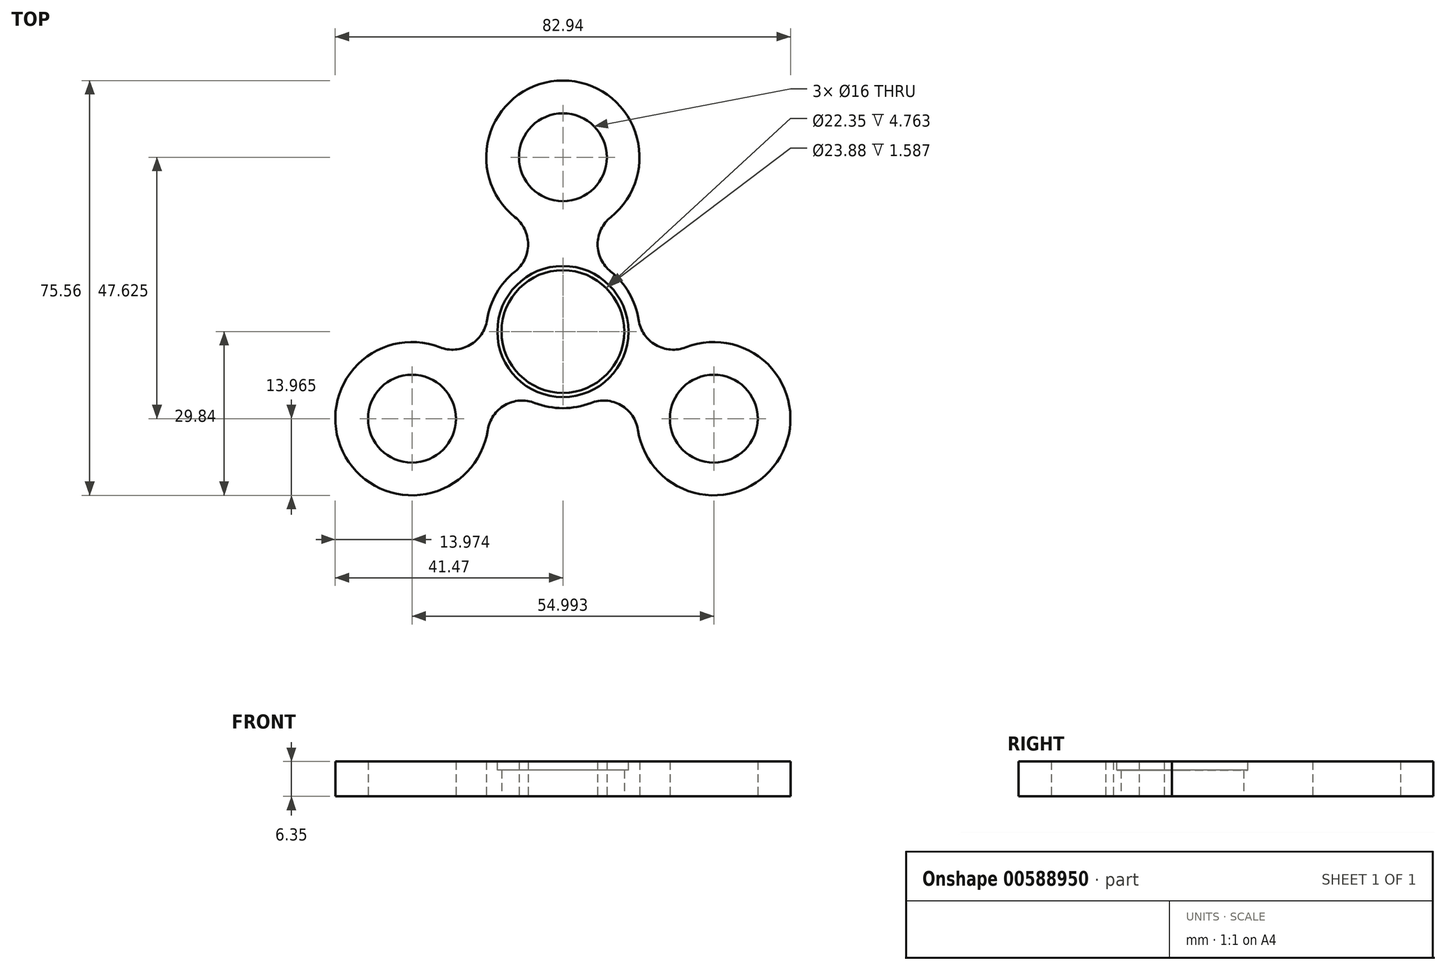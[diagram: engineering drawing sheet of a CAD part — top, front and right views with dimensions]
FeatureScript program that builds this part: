
annotation { "Feature Type Name" : "Feature", "Feature Type Description" : "" }
export const myFeature = defineFeature(function(context is Context, id is Id, definition is map)
    precondition{}
    {
        {
            var Q0;
            Q0=qCreatedBy(makeId("Top.planeOp"),FACE);
            var sketch = newSketch(context, id + "F0", { "sketchPlane" : qUnion([Q0])});
            skCircle(sketch, "E0", {"center": v(0, 0) * mm, "radius": 11.18 * mm});
            skArc(sketch, "E1", {"start": v(-8.72, 10.91) * mm, "mid": v(-12.1, 6.98) * mm, "end": v(-13.81, 2.1) * mm});
            skCircle(sketch, "E2", {"center": v(0, 31.75) * mm, "radius": 8 * mm});
            skArc(sketch, "E3", {"start": v(8.72, 20.84) * mm, "mid": v(0, 45.72) * mm, "end": v(-8.72, 20.84) * mm});
            skArc(sketch, "E4", {"start": v(-8.72, 10.91) * mm, "mid": v(-6.33, 15.87) * mm, "end": v(-8.72, 20.84) * mm});
            skArc(sketch, "E5.MirrorCS", {"start": v(8.72, 10.91) * mm, "mid": v(6.33, 15.87) * mm, "end": v(8.72, 20.84) * mm});
            skArc(sketch, "E6.1.0", {"start": v(-13.81, 2.1) * mm, "mid": v(-16.92, -2.45) * mm, "end": v(-22.4, -2.87) * mm});
            skArc(sketch, "E6.1.1", {"start": v(-5.1, -13) * mm, "mid": v(-10.58, -13.42) * mm, "end": v(-13.68, -17.97) * mm});
            skArc(sketch, "E6.1.2", {"start": v(-22.4, -2.87) * mm, "mid": v(-39.6, -22.86) * mm, "end": v(-13.68, -17.97) * mm});
            skCircle(sketch, "E6.1.3", {"center": v(-27.5, -15.87) * mm, "radius": 8 * mm});
            skArc(sketch, "E6.2.0", {"start": v(5.1, -13) * mm, "mid": v(10.58, -13.42) * mm, "end": v(13.68, -17.97) * mm});
            skArc(sketch, "E6.2.1", {"start": v(13.81, 2.1) * mm, "mid": v(16.92, -2.45) * mm, "end": v(22.4, -2.87) * mm});
            skArc(sketch, "E6.2.2", {"start": v(13.68, -17.97) * mm, "mid": v(39.6, -22.86) * mm, "end": v(22.4, -2.87) * mm});
            skCircle(sketch, "E6.2.3", {"center": v(27.5, -15.88) * mm, "radius": 8 * mm});
            skArc(sketch, "E7.trimOffspring", {"start": v(13.81, 2.1) * mm, "mid": v(12.1, 6.98) * mm, "end": v(8.72, 10.91) * mm});
            skArc(sketch, "E8.trimOffspring", {"start": v(-5.1, -13) * mm, "mid": v(0, -13.97) * mm, "end": v(5.1, -13) * mm});
            skSolve(sketch);
        }
        {
            var Q0;
            Q0=makeQuery(id+"F0.imprint","IMPRINT",FACE,{"disambiguationData":[TD([[makeQuery(id+"F0.imprint","IMPRINT",EDGE,{"derivedFrom":sQuery(id+"F0.wireOp",EDGE,"E0")}),-1.0]])]});
            extrude(context, id + "F1", {"entities" : qUnion([Q0]), "depth" : 6.35 * mm, "offsetDistance" : 25.4 * mm});
        }
        {
            var Q0;
            Q0=makeQuery(id+"F1.opExtrude","CAP_FACE",FACE,{"disambiguationData":[OSD([sQuery(id+"F0.wireOp",EDGE,"E0"),sQuery(id+"F0.wireOp",EDGE,"E1"),sQuery(id+"F0.wireOp",EDGE,"E2"),sQuery(id+"F0.wireOp",EDGE,"E3"),sQuery(id+"F0.wireOp",EDGE,"E4"),sQuery(id+"F0.wireOp",EDGE,"E5.MirrorCS"),sQuery(id+"F0.wireOp",EDGE,"E6.1.0"),sQuery(id+"F0.wireOp",EDGE,"E6.1.1"),sQuery(id+"F0.wireOp",EDGE,"E6.1.2"),sQuery(id+"F0.wireOp",EDGE,"E6.1.3"),sQuery(id+"F0.wireOp",EDGE,"E6.2.0"),sQuery(id+"F0.wireOp",EDGE,"E6.2.1"),sQuery(id+"F0.wireOp",EDGE,"E6.2.2"),sQuery(id+"F0.wireOp",EDGE,"E6.2.3"),sQuery(id+"F0.wireOp",EDGE,"E7.trimOffspring"),sQuery(id+"F0.wireOp",EDGE,"E8.trimOffspring")])],"isStart":false});
            var sketch = newSketch(context, id + "F2", { "sketchPlane" : qUnion([Q0])});
            skCircle(sketch, "E9", {"center": v(0, 0) * mm, "radius": 11.94 * mm});
            skSolve(sketch);
        }
        {
            var Q0;
            Q0 = qSketchRegion(id + "F2", true);
            extrude(context, id + "F3", {"entities" : qUnion([Q0]), "operationType" : NewBodyOperationType.REMOVE, "oppositeDirection" : true, "depth" : 1.59 * mm, "offsetDistance" : 25.4 * mm});
        }
    });
